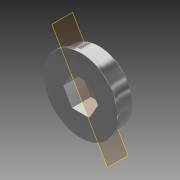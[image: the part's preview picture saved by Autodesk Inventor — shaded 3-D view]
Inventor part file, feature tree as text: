
AUTODESK INVENTOR PART (.ipt)
format: ipt  version: 2016 SP1 (Build 200210100, 210)  size: 136,704 bytes
history: native  units: in
note: dims shown in document units (in); Inventor stores cm internally (conversion verified against a paired STEP export)
features: plane x1, fillet x1
ambient origin geometry x8: Origin, YZ Plane, XZ Plane, XY Plane, X Axis, Y Axis, Z Axis, Center Point
bodies: Solid1 (feature_tree)
feature tree (2):
  plane  "Work Plane1"
  fillet  "Fillet2"  [1 undecoded]
note: 1 required parameter value undecoded (feature->parameter linkage not recoverable at this tier; creation-order binding heuristic only, values carry confidence <= 0.55)
